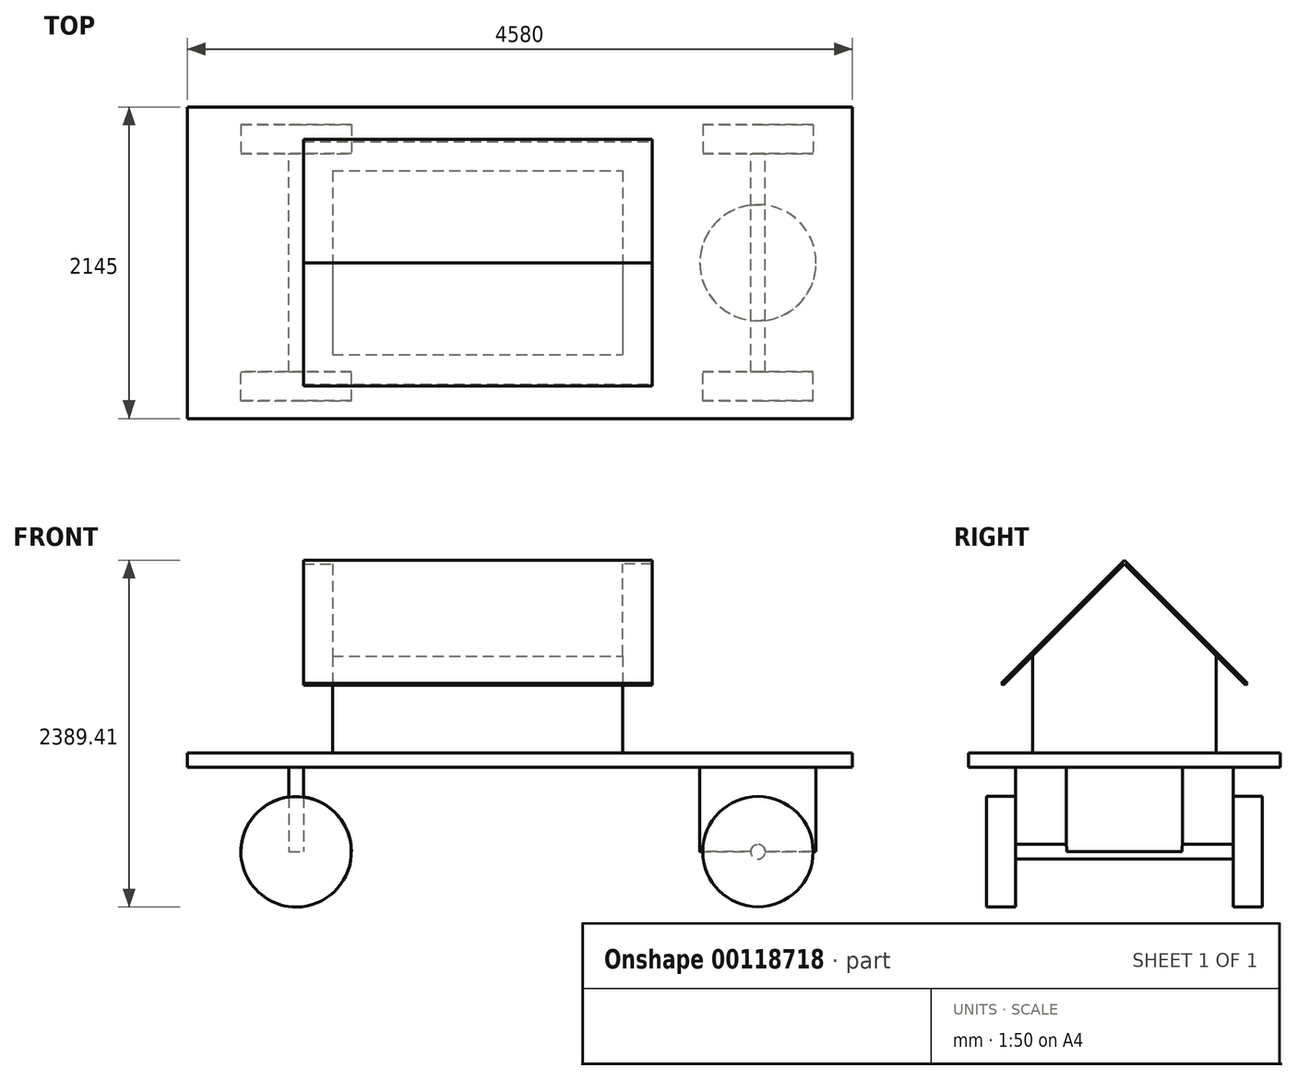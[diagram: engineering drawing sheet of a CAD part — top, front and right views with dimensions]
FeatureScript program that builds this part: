
annotation { "Feature Type Name" : "Feature", "Feature Type Description" : "" }
export const myFeature = defineFeature(function(context is Context, id is Id, definition is map)
    precondition{}
    {
        {
            var Q0;
            Q0=qCreatedBy(makeId("Top.planeOp"),FACE);
            var sketch = newSketch(context, id + "F0", { "sketchPlane" : qUnion([Q0])});
            skLineSegment(sketch, "E0.bottom", {"start": v(-2290, 1072.5) * mm, "end": v(2290, 1072.5) * mm});
            skLineSegment(sketch, "E0.top", {"start": v(-2290, -1072.5) * mm, "end": v(2290, -1072.5) * mm});
            skLineSegment(sketch, "E0.left", {"start": v(-2290, 1072.5) * mm, "end": v(-2290, -1072.5) * mm});
            skLineSegment(sketch, "E0.right", {"start": v(2290, 1072.5) * mm, "end": v(2290, -1072.5) * mm});
            skSolve(sketch);
        }
        {
            var Q0;
            Q0=makeQuery(id+"F0.imprint","IMPRINT",FACE,{"disambiguationData":[TD([[makeQuery(id+"F0.imprint","IMPRINT",EDGE,{"derivedFrom":sQuery(id+"F0.wireOp",EDGE,"E0.bottom")}),-1.0]])]});
            extrude(context, id + "F1", {"entities" : qUnion([Q0]), "depth" : 100 * mm});
        }
        {
            var Q0;
            Q0=qCreatedBy(makeId("Front.planeOp"),FACE);
            var sketch = newSketch(context, id + "F2", { "sketchPlane" : qUnion([Q0])});
            skLineSegment(sketch, "E1.bottom", {"start": v(-1590, 0) * mm, "end": v(-1490, 0) * mm});
            skLineSegment(sketch, "E1.top", {"start": v(-1590, -580) * mm, "end": v(-1490, -580) * mm});
            skLineSegment(sketch, "E1.left", {"start": v(-1590, 0) * mm, "end": v(-1590, -580) * mm});
            skLineSegment(sketch, "E1.right", {"start": v(-1490, 0) * mm, "end": v(-1490, -580) * mm});
            skSolve(sketch);
        }
        {
            var Q0;
            Q0 = qSketchRegion(id + "F5", true);
            var Q1;
            Q1=makeQuery(id+"F2.imprint","IMPRINT",FACE,{"disambiguationData":[TD([[makeQuery(id+"F2.imprint","IMPRINT",EDGE,{"derivedFrom":sQuery(id+"F2.wireOp",EDGE,"E1.bottom")}),-1.0]])]});
            extrude(context, id + "F3", {"entities" : qUnion([Q0, Q1]), "operationType" : NewBodyOperationType.ADD, "endBound" : BoundingType.SYMMETRIC, "depth" : 900 * mm});
        }
        {
            var Q0;
            Q0=makeQuery(id+"F2.imprint","IMPRINT",FACE,{"disambiguationData":[TD([[makeQuery(id+"F2.imprint","IMPRINT",EDGE,{"derivedFrom":sQuery(id+"F2.wireOp",EDGE,"E1.bottom")}),-1.0]])]});
            extrude(context, id + "F4", {"entities" : qUnion([Q0]), "operationType" : NewBodyOperationType.ADD, "endBound" : BoundingType.SYMMETRIC, "depth" : 1500 * mm});
        }
        {
            var Q0;
            Q0=makeQuery(id+"F4.opExtrude","CAP_FACE",FACE,{"disambiguationData":[OSD([sQuery(id+"F2.wireOp",EDGE,"E1.bottom"),sQuery(id+"F2.wireOp",EDGE,"E1.top"),sQuery(id+"F2.wireOp",EDGE,"E1.left"),sQuery(id+"F2.wireOp",EDGE,"E1.right")])],"isStart":false});
            var sketch = newSketch(context, id + "F5", { "sketchPlane" : qUnion([Q0])});
            skCircle(sketch, "E2", {"center": v(-1540, -581.13) * mm, "radius": 380 * mm});
            skSolve(sketch);
        }
        {
            var Q0;
            {var subQ5=makeQuery(id+"F4.opExtrude","CAP_EDGE",EDGE,{"disambiguationData":[OSD([sQuery(id+"F2.wireOp",EDGE,"E1.top")])],"isStart":false});Q0=makeQuery(id+"F5.imprint","IMPRINT",FACE,{"disambiguationData":[TD([[makeQuery(id+"F5.imprint","IMPRINT",EDGE,{"derivedFrom":subQ5}),-1.0]])]});}
            var Q1;
            {var subQ5=makeQuery(id+"F4.opExtrude","CAP_EDGE",EDGE,{"disambiguationData":[OSD([sQuery(id+"F2.wireOp",EDGE,"E1.top")])],"isStart":false});Q1=makeQuery(id+"F5.imprint","IMPRINT",FACE,{"disambiguationData":[TD([[makeQuery(id+"F5.imprint","IMPRINT",EDGE,{"derivedFrom":subQ5}),1.0]])]});}
            extrude(context, id + "F6", {"entities" : qUnion([Q0, Q1]), "operationType" : NewBodyOperationType.ADD, "depth" : 200 * mm});
        }
        {
            var Q0;
            Q0=makeQuery(id+"F4.opExtrude","CAP_FACE",FACE,{"disambiguationData":[OSD([sQuery(id+"F2.wireOp",EDGE,"E1.bottom"),sQuery(id+"F2.wireOp",EDGE,"E1.top"),sQuery(id+"F2.wireOp",EDGE,"E1.left"),sQuery(id+"F2.wireOp",EDGE,"E1.right")])],"isStart":true});
            var sketch = newSketch(context, id + "F7", { "sketchPlane" : qUnion([Q0])});
            skCircle(sketch, "E3", {"center": v(1540, -580) * mm, "radius": 380 * mm});
            skSolve(sketch);
        }
        {
            var Q0;
            {var subQ5=makeQuery(id+"F4.opExtrude","CAP_EDGE",EDGE,{"disambiguationData":[OSD([sQuery(id+"F2.wireOp",EDGE,"E1.top")])],"isStart":true});Q0=makeQuery(id+"F7.imprint","IMPRINT",FACE,{"disambiguationData":[TD([[makeQuery(id+"F7.imprint","IMPRINT",EDGE,{"derivedFrom":subQ5}),-1.0]])]});}
            var Q1;
            {var subQ5=makeQuery(id+"F4.opExtrude","CAP_EDGE",EDGE,{"disambiguationData":[OSD([sQuery(id+"F2.wireOp",EDGE,"E1.top")])],"isStart":true});Q1=makeQuery(id+"F7.imprint","IMPRINT",FACE,{"disambiguationData":[TD([[makeQuery(id+"F7.imprint","IMPRINT",EDGE,{"derivedFrom":subQ5}),1.0]])]});}
            extrude(context, id + "F8", {"entities" : qUnion([Q0, Q1]), "operationType" : NewBodyOperationType.ADD, "depth" : 200 * mm});
        }
        {
            var Q0;
            Q0=makeQuery(id+"F1.opExtrude","CAP_FACE",FACE,{"disambiguationData":[OSD([sQuery(id+"F0.wireOp",EDGE,"E0.bottom"),sQuery(id+"F0.wireOp",EDGE,"E0.top"),sQuery(id+"F0.wireOp",EDGE,"E0.left"),sQuery(id+"F0.wireOp",EDGE,"E0.right")])],"isStart":true});
            var sketch = newSketch(context, id + "F9", { "sketchPlane" : qUnion([Q0])});
            skCircle(sketch, "E4", {"center": v(1640, 0) * mm, "radius": 400 * mm});
            skSolve(sketch);
        }
        {
            var Q0;
            Q0=makeQuery(id+"F9.imprint","IMPRINT",FACE,{"disambiguationData":[TD([[makeQuery(id+"F9.imprint","IMPRINT",EDGE,{"derivedFrom":sQuery(id+"F9.wireOp",EDGE,"E4")}),1.0]])]});
            extrude(context, id + "F10", {"entities" : qUnion([Q0]), "operationType" : NewBodyOperationType.ADD, "depth" : 580 * mm});
        }
        {
            var Q0;
            Q0=qCreatedBy(makeId("Front.planeOp"),FACE);
            var sketch = newSketch(context, id + "F11", { "sketchPlane" : qUnion([Q0])});
            skCircle(sketch, "E5", {"center": v(1640, -580) * mm, "radius": 50 * mm});
            skSolve(sketch);
        }
        {
            var Q0;
            Q0=makeQuery(id+"F11.imprint","IMPRINT",FACE,{"disambiguationData":[TD([[makeQuery(id+"F11.imprint","IMPRINT",EDGE,{"derivedFrom":sQuery(id+"F11.wireOp",EDGE,"E5")}),1.0]])]});
            extrude(context, id + "F12", {"entities" : qUnion([Q0]), "operationType" : NewBodyOperationType.ADD, "endBound" : BoundingType.SYMMETRIC, "depth" : 1500 * mm});
        }
        {
            var Q0;
            Q0=makeQuery(id+"F12.opExtrude","CAP_FACE",FACE,{"disambiguationData":[OSD([sQuery(id+"F11.wireOp",EDGE,"E5")])],"isStart":false});
            var sketch = newSketch(context, id + "F13", { "sketchPlane" : qUnion([Q0])});
            skCircle(sketch, "E6", {"center": v(1640, -580) * mm, "radius": 380 * mm});
            skSolve(sketch);
        }
        {
            var Q0;
            Q0=makeQuery(id+"F13.imprint","IMPRINT",FACE,{"disambiguationData":[TD([[makeQuery(id+"F13.imprint","IMPRINT",EDGE,{"derivedFrom":sQuery(id+"F13.wireOp",EDGE,"E6")}),1.0]])]});
            var Q1;
            Q1=makeQuery(id+"F13.imprint","IMPRINT",FACE,{"disambiguationData":[TD([[makeQuery(id+"F13.imprint","IMPRINT",EDGE,{"derivedFrom":makeQuery(id+"F12.opExtrude","CAP_EDGE",EDGE,{"disambiguationData":[OSD([sQuery(id+"F11.wireOp",EDGE,"E5")])],"isStart":false})}),1.0]])]});
            extrude(context, id + "F14", {"entities" : qUnion([Q0, Q1]), "operationType" : NewBodyOperationType.ADD, "depth" : 200 * mm});
        }
        {
            var Q0;
            Q0=makeQuery(id+"F12.opExtrude","CAP_FACE",FACE,{"disambiguationData":[OSD([sQuery(id+"F11.wireOp",EDGE,"E5")])],"isStart":true});
            var sketch = newSketch(context, id + "F15", { "sketchPlane" : qUnion([Q0])});
            skCircle(sketch, "E7", {"center": v(-1640, -580) * mm, "radius": 380 * mm});
            skSolve(sketch);
        }
        {
            var Q0;
            Q0=makeQuery(id+"F15.imprint","IMPRINT",FACE,{"disambiguationData":[TD([[makeQuery(id+"F15.imprint","IMPRINT",EDGE,{"derivedFrom":sQuery(id+"F15.wireOp",EDGE,"E7")}),1.0]])]});
            var Q1;
            Q1=makeQuery(id+"F15.imprint","IMPRINT",FACE,{"disambiguationData":[TD([[makeQuery(id+"F15.imprint","IMPRINT",EDGE,{"derivedFrom":makeQuery(id+"F12.opExtrude","CAP_EDGE",EDGE,{"disambiguationData":[OSD([sQuery(id+"F11.wireOp",EDGE,"E5")])],"isStart":true})}),-1.0]])]});
            extrude(context, id + "F16", {"entities" : qUnion([Q0, Q1]), "operationType" : NewBodyOperationType.ADD, "depth" : 200 * mm});
        }
        {
            var Q0;
            Q0=makeQuery(id+"F1.opExtrude","CAP_FACE",FACE,{"disambiguationData":[OSD([sQuery(id+"F0.wireOp",EDGE,"E0.bottom"),sQuery(id+"F0.wireOp",EDGE,"E0.top"),sQuery(id+"F0.wireOp",EDGE,"E0.left"),sQuery(id+"F0.wireOp",EDGE,"E0.right")])],"isStart":false});
            var sketch = newSketch(context, id + "F17", { "sketchPlane" : qUnion([Q0])});
            skLineSegment(sketch, "E8.bottom", {"start": v(-1290, 632.5) * mm, "end": v(710, 632.5) * mm});
            skLineSegment(sketch, "E8.top", {"start": v(-1290, -632.5) * mm, "end": v(710, -632.5) * mm});
            skLineSegment(sketch, "E8.left", {"start": v(-1290, 632.5) * mm, "end": v(-1290, -632.5) * mm});
            skLineSegment(sketch, "E8.right", {"start": v(710, 632.5) * mm, "end": v(710, -632.5) * mm});
            skSolve(sketch);
        }
        {
            var Q0;
            Q0=makeQuery(id+"F17.imprint","IMPRINT",FACE,{"disambiguationData":[TD([[makeQuery(id+"F17.imprint","IMPRINT",EDGE,{"derivedFrom":sQuery(id+"F17.wireOp",EDGE,"E8.bottom")}),-1.0]])]});
            extrude(context, id + "F18", {"entities" : qUnion([Q0]), "operationType" : NewBodyOperationType.ADD, "depth" : 2000 * mm});
        }
        {
            var Q0;
            Q0=makeQuery(id+"F18.opExtrude","SWEPT_FACE",FACE,{"disambiguationData":[OSD([sQuery(id+"F17.wireOp",EDGE,"E8.right")])]});
            var sketch = newSketch(context, id + "F19", { "sketchPlane" : qUnion([Q0])});
            skLineSegment(sketch, "E9", {"start": v(0, 2100) * mm, "end": v(0, 100) * mm, "construction": true});
            skLineSegment(sketch, "E10", {"start": v(0, 1400) * mm, "end": v(-824.22, 575.78) * mm});
            skLineSegment(sketch, "E11", {"start": v(-824.22, 575.78) * mm, "end": v(-824.22, 2239.17) * mm});
            skLineSegment(sketch, "E12", {"start": v(-824.22, 2239.17) * mm, "end": v(998.34, 2239.17) * mm});
            skLineSegment(sketch, "E13", {"start": v(998.34, 2239.17) * mm, "end": v(998.34, 401.66) * mm});
            skLineSegment(sketch, "E14", {"start": v(998.34, 401.66) * mm, "end": v(0, 1400) * mm});
            skSolve(sketch);
        }
        {
            var Q0;
            {var subQ0=sQuery(id+"F19.wireOp",EDGE,"E11");Q0=makeQuery(id+"F19.imprint","IMPRINT",FACE,{"disambiguationData":[TD([[makeQuery(id+"F19.imprint","IMPRINT",EDGE,{"derivedFrom":subQ0}),-1.0]])]});}
            var Q1;
            {var subQ0=sQuery(id+"F17.wireOp",EDGE,"E8.right");var subQ1=makeQuery(id+"F18.opExtrude","CAP_EDGE",EDGE,{"disambiguationData":[OSD([subQ0])],"isStart":false});Q1=makeQuery(id+"F19.imprint","IMPRINT",FACE,{"disambiguationData":[TD([[makeQuery(id+"F19.imprint","IMPRINT",EDGE,{"derivedFrom":subQ1}),1.0]])]});}
            extrude(context, id + "F20", {"entities" : qUnion([Q0, Q1]), "operationType" : NewBodyOperationType.REMOVE, "oppositeDirection" : true, "depth" : 2000 * mm});
        }
        {
            var Q0;
            Q0=makeQuery(id+"F18.opExtrude","SWEPT_FACE",FACE,{"disambiguationData":[OSD([sQuery(id+"F17.wireOp",EDGE,"E8.right")])]});
            var sketch = newSketch(context, id + "F21", { "sketchPlane" : qUnion([Q0])});
            skLineSegment(sketch, "E15", {"start": v(0, 1400) * mm, "end": v(-834.39, 565.61) * mm});
            skLineSegment(sketch, "E16", {"start": v(-834.39, 565.61) * mm, "end": v(-848.53, 579.76) * mm});
            skLineSegment(sketch, "E17", {"start": v(-848.53, 579.76) * mm, "end": v(0, 1428.28) * mm});
            skLineSegment(sketch, "E18", {"start": v(0, 1428.28) * mm, "end": v(848.53, 579.76) * mm});
            skLineSegment(sketch, "E19", {"start": v(848.53, 579.76) * mm, "end": v(834.39, 565.61) * mm});
            skLineSegment(sketch, "E20", {"start": v(834.39, 565.61) * mm, "end": v(0, 1400) * mm});
            skSolve(sketch);
        }
        {
            var Q0;
            {var subQ0=sQuery(id+"F21.wireOp",EDGE,"E16");Q0=makeQuery(id+"F21.imprint","IMPRINT",FACE,{"disambiguationData":[TD([[makeQuery(id+"F21.imprint","IMPRINT",EDGE,{"derivedFrom":subQ0}),-1.0]])]});}
            extrude(context, id + "F22", {"entities" : qUnion([Q0]), "operationType" : NewBodyOperationType.ADD, "oppositeDirection" : true, "depth" : 2200 * mm});
        }
        {
            var Q0;
            Q0 = qSketchRegion(id + "F21", true);
            extrude(context, id + "F23", {"entities" : qUnion([Q0]), "operationType" : NewBodyOperationType.ADD, "depth" : 200 * mm});
        }
    });
